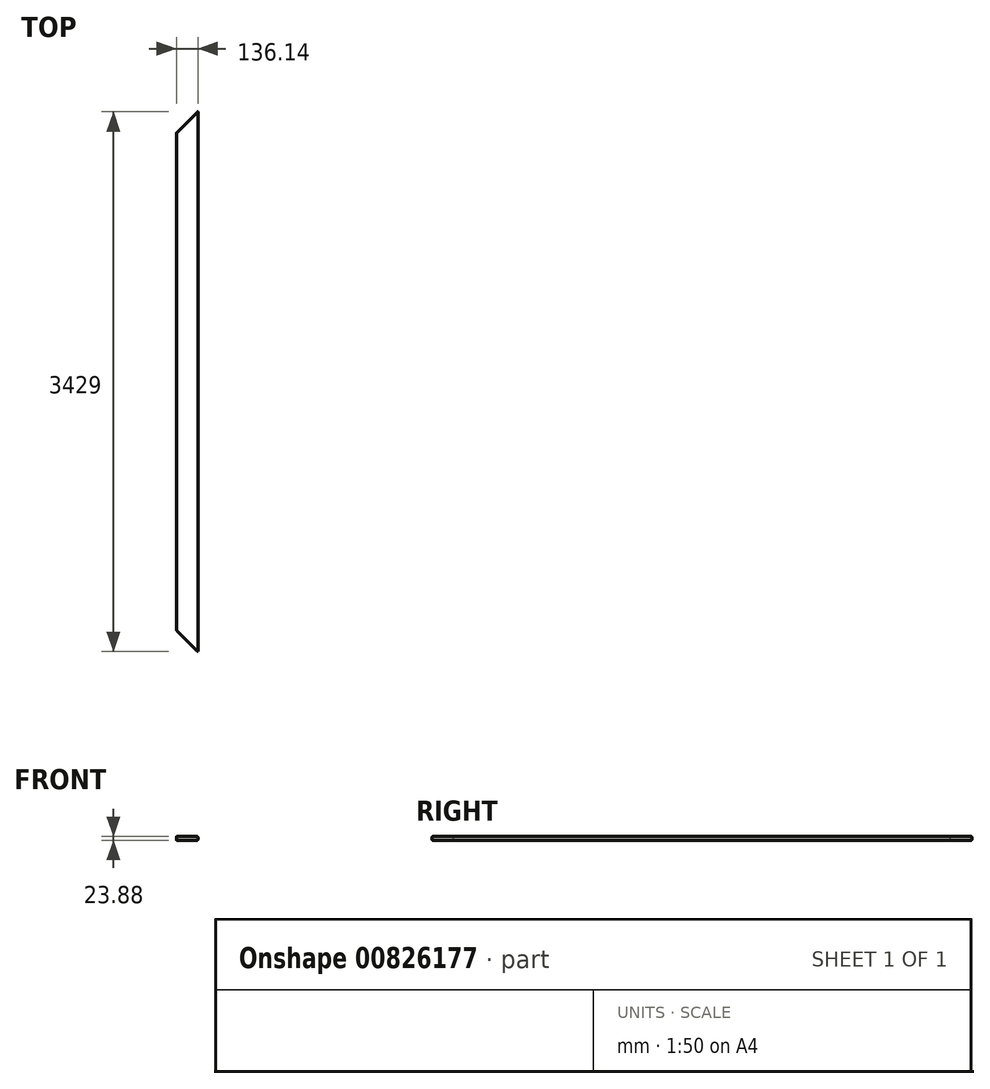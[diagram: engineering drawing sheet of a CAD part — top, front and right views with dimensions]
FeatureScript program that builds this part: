
annotation { "Feature Type Name" : "Feature", "Feature Type Description" : "" }
export const myFeature = defineFeature(function(context is Context, id is Id, definition is map)
    precondition{}
    {
        {
            var Q0;
            Q0=qCreatedBy(makeId("Front.planeOp"),FACE);
            var sketch = newSketch(context, id + "F0", { "sketchPlane" : qUnion([Q0])});
            skLineSegment(sketch, "E0.bottom", {"start": v(-63.25, 11.94) * mm, "end": v(63.25, 11.94) * mm});
            skLineSegment(sketch, "E0.top", {"start": v(-63.25, -11.94) * mm, "end": v(63.25, -11.94) * mm});
            skLineSegment(sketch, "E0.left", {"start": v(-68.07, 7.11) * mm, "end": v(-68.07, -7.11) * mm});
            skLineSegment(sketch, "E0.right", {"start": v(68.07, 7.11) * mm, "end": v(68.07, -7.11) * mm});
            skPoint(sketch, "E0.middle", {"position": v(0, 0) * mm});
            skPoint(sketch, "E1.visualSharp", {"position": v(-68.07, 11.94) * mm});
            skArc(sketch, "E1.filletArc", {"start": v(-63.25, 11.94) * mm, "mid": v(-66.66, 10.52) * mm, "end": v(-68.07, 7.11) * mm});
            skPoint(sketch, "E2.visualSharp", {"position": v(68.07, 11.94) * mm});
            skArc(sketch, "E2.filletArc", {"start": v(68.07, 7.11) * mm, "mid": v(66.66, 10.52) * mm, "end": v(63.25, 11.94) * mm});
            skPoint(sketch, "E3.visualSharp", {"position": v(68.07, -11.94) * mm});
            skArc(sketch, "E3.filletArc", {"start": v(63.25, -11.94) * mm, "mid": v(66.66, -10.52) * mm, "end": v(68.07, -7.11) * mm});
            skPoint(sketch, "E4.visualSharp", {"position": v(-68.07, -11.94) * mm});
            skArc(sketch, "E4.filletArc", {"start": v(-68.07, -7.11) * mm, "mid": v(-66.66, -10.52) * mm, "end": v(-63.25, -11.94) * mm});
            skSolve(sketch);
        }
        {
            var Q0;
            Q0=makeQuery(id+"F0.imprint","IMPRINT",FACE,{"disambiguationData":[TD([[makeQuery(id+"F0.imprint","IMPRINT",EDGE,{"derivedFrom":sQuery(id+"F0.wireOp",EDGE,"E0.bottom")}),-1.0]])]});
            extrude(context, id + "F1", {"entities" : qUnion([Q0]), "endBound" : BoundingType.SYMMETRIC, "depth" : 3429 * mm, "offsetDistance" : 25.4 * mm});
        }
        {
            var Q0;
            Q0=makeQuery(id+"F1.opExtrude","SWEPT_FACE",FACE,{"disambiguationData":[OSD([sQuery(id+"F0.wireOp",EDGE,"E0.bottom")])]});
            var sketch = newSketch(context, id + "F2", { "sketchPlane" : qUnion([Q0])});
            skLineSegment(sketch, "E5", {"start": v(-68.07, -1578.36) * mm, "end": v(-68.07, -1714.5) * mm});
            skLineSegment(sketch, "E6", {"start": v(68.07, -1714.5) * mm, "end": v(-68.07, -1714.5) * mm});
            skLineSegment(sketch, "E7", {"start": v(-68.07, -1578.36) * mm, "end": v(68.07, -1714.5) * mm});
            skLineSegment(sketch, "E8.MirrorCS", {"start": v(-68.07, 1578.36) * mm, "end": v(-68.07, 1714.5) * mm});
            skLineSegment(sketch, "E9.MirrorCS", {"start": v(68.07, 1714.5) * mm, "end": v(-68.07, 1714.5) * mm});
            skLineSegment(sketch, "E10.MirrorCS", {"start": v(-68.07, 1578.36) * mm, "end": v(68.07, 1714.5) * mm});
            skSolve(sketch);
        }
        {
            var Q0;
            Q0=qSketchRegion(id+"F2",true);
            extrude(context, id + "F3", {"entities" : qUnion([Q0]), "operationType" : NewBodyOperationType.REMOVE, "endBound" : BoundingType.THROUGH_ALL, "oppositeDirection" : true, "depth" : 25.4 * mm, "offsetDistance" : 25.4 * mm});
        }
    });
